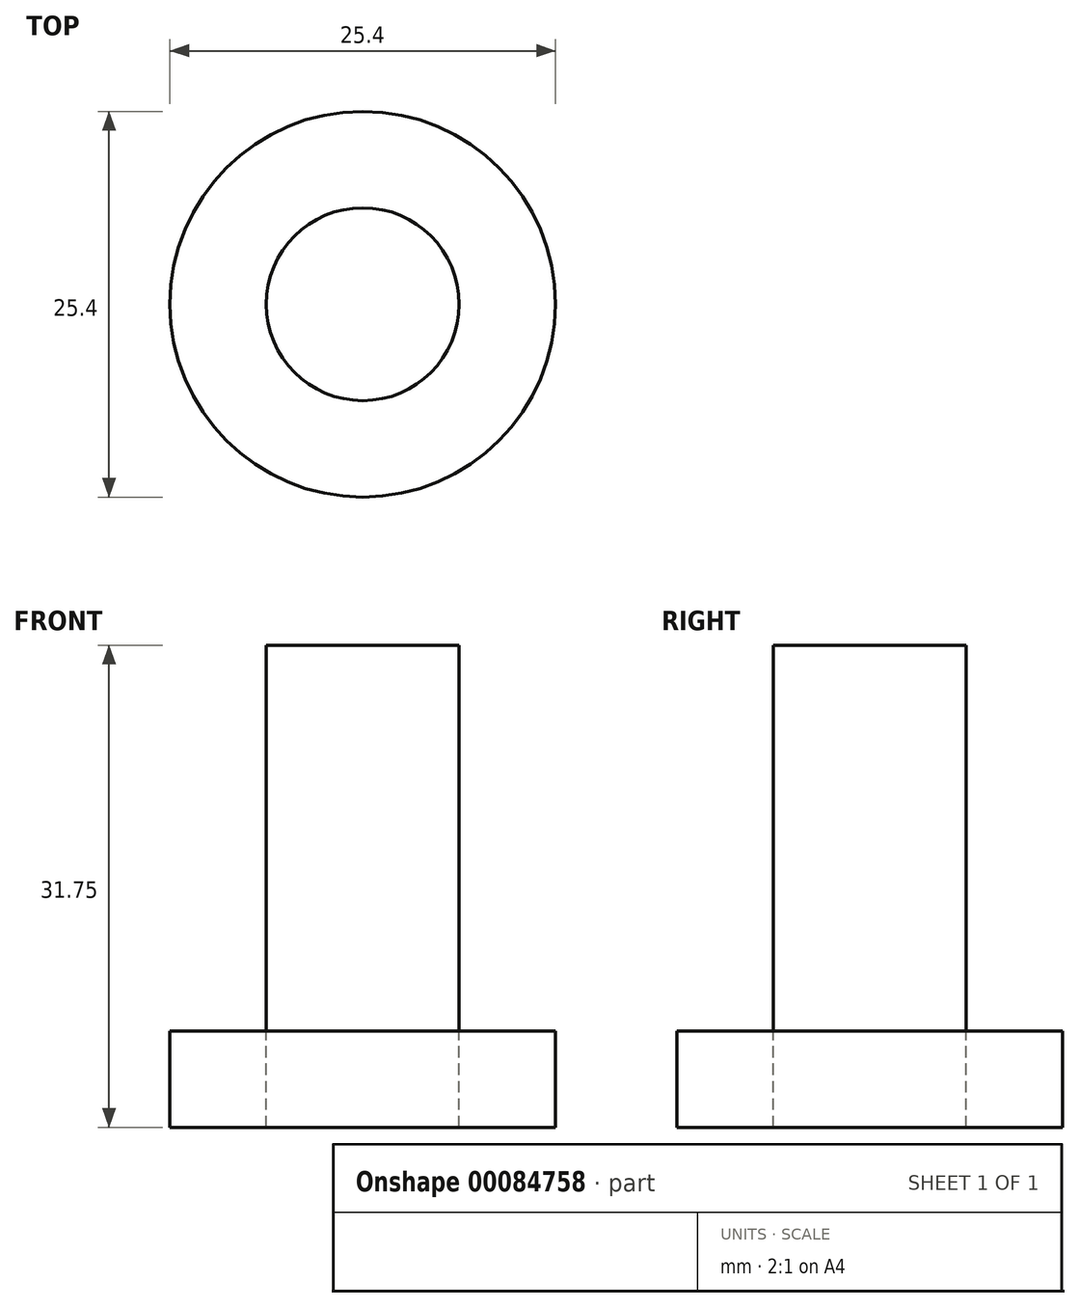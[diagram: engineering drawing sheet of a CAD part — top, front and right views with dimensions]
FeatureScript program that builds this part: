
annotation { "Feature Type Name" : "Feature", "Feature Type Description" : "" }
export const myFeature = defineFeature(function(context is Context, id is Id, definition is map)
    precondition{}
    {
        {
            var Q0;
            Q0=qCreatedBy(makeId("Top.planeOp"),FACE);
            var sketch = newSketch(context, id + "F0", { "sketchPlane" : qUnion([Q0])});
            skCircle(sketch, "E0", {"center": v(0, 0) * mm, "radius": 6.35 * mm});
            skCircle(sketch, "E1", {"center": v(0, 0) * mm, "radius": 12.7 * mm});
            skSolve(sketch);
        }
        {
            var Q0;
            Q0=makeQuery(id+"F0.imprint","IMPRINT",FACE,{"disambiguationData":[TD([[makeQuery(id+"F0.imprint","IMPRINT",EDGE,{"derivedFrom":sQuery(id+"F0.wireOp",EDGE,"E0")}),1.0]])]});
            extrude(context, id + "F1", {"entities" : qUnion([Q0]), "depth" : 25.4 * mm});
        }
        {
            var Q0;
            Q0 = qSketchRegion(id + "F0", true);
            extrude(context, id + "F2", {"entities" : qUnion([Q0]), "oppositeDirection" : true, "depth" : 6.35 * mm});
        }
    });
